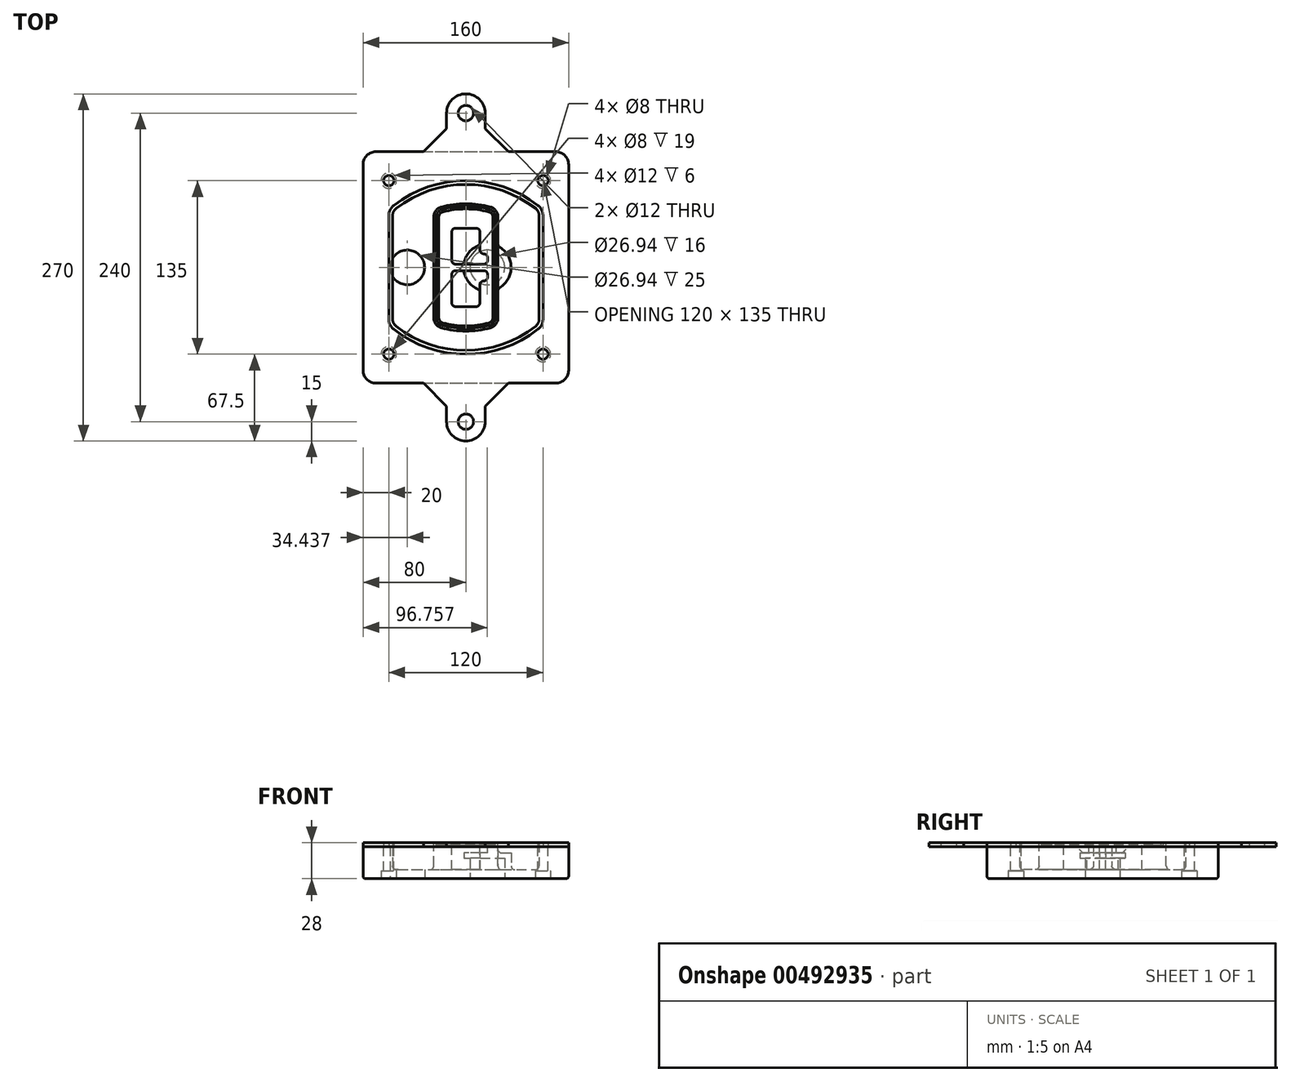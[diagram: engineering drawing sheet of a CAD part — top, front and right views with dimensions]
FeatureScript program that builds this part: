
annotation { "Feature Type Name" : "Feature", "Feature Type Description" : "" }
export const myFeature = defineFeature(function(context is Context, id is Id, definition is map)
    precondition{}
    {
        {
            var Q0;
            Q0=qCreatedBy(makeId("Top.planeOp"),FACE);
            var sketch = newSketch(context, id + "F0", { "sketchPlane" : qUnion([Q0])});
            skPoint(sketch, "E0.rect.middle", {"position": v(0, 0) * mm});
            skLineSegment(sketch, "E1.bottom", {"start": v(-70, -90) * mm, "end": v(70, -90) * mm});
            skLineSegment(sketch, "E1.top", {"start": v(-70, 90) * mm, "end": v(70, 90) * mm});
            skLineSegment(sketch, "E1.left", {"start": v(-80, -80) * mm, "end": v(-80, 80) * mm});
            skLineSegment(sketch, "E1.right", {"start": v(80, -80) * mm, "end": v(80, 80) * mm});
            skLineSegment(sketch, "E2", {"start": v(-80, 90) * mm, "end": v(80, -90) * mm, "construction": true});
            skLineSegment(sketch, "E3", {"start": v(80, 90) * mm, "end": v(-80, -90) * mm, "construction": true});
            skCircle(sketch, "E4", {"center": v(-60, 67.5) * mm, "radius": 4 * mm});
            skCircle(sketch, "E5", {"center": v(60, 67.5) * mm, "radius": 4 * mm});
            skCircle(sketch, "E6", {"center": v(60, -67.5) * mm, "radius": 4 * mm});
            skCircle(sketch, "E7", {"center": v(-60, -67.5) * mm, "radius": 4 * mm});
            skLineSegment(sketch, "E8", {"start": v(-60, 67.5) * mm, "end": v(60, 67.5) * mm, "construction": true});
            skLineSegment(sketch, "E9", {"start": v(60, 67.5) * mm, "end": v(60, -67.5) * mm, "construction": true});
            skLineSegment(sketch, "E10", {"start": v(60, -67.5) * mm, "end": v(-60, -67.5) * mm, "construction": true});
            skLineSegment(sketch, "E11", {"start": v(-60, -67.5) * mm, "end": v(-60, 67.5) * mm, "construction": true});
            skLineSegment(sketch, "E12", {"start": v(-60, 40.3) * mm, "end": v(-60, -40.3) * mm});
            skLineSegment(sketch, "E13", {"start": v(60, 40.3) * mm, "end": v(60, -40.3) * mm});
            skArc(sketch, "E14", {"start": v(56.15, 48.18) * mm, "mid": v(0, 67.5) * mm, "end": v(-56.15, 48.18) * mm});
            skArc(sketch, "E15", {"start": v(-56.15, -48.18) * mm, "mid": v(0, -67.5) * mm, "end": v(56.15, -48.18) * mm});
            skLineSegment(sketch, "E16", {"start": v(-60, 0) * mm, "end": v(60, 0) * mm, "construction": true});
            skPoint(sketch, "E17.visualSharp", {"position": v(-60, -45) * mm});
            skArc(sketch, "E17.filletArc", {"start": v(-60, -40.3) * mm, "mid": v(-58.99, -44.68) * mm, "end": v(-56.15, -48.18) * mm});
            skPoint(sketch, "E18.visualSharp", {"position": v(-60, 45) * mm});
            skArc(sketch, "E18.filletArc", {"start": v(-56.15, 48.18) * mm, "mid": v(-58.99, 44.68) * mm, "end": v(-60, 40.3) * mm});
            skPoint(sketch, "E19.visualSharp", {"position": v(60, 45) * mm});
            skArc(sketch, "E19.filletArc", {"start": v(60, 40.3) * mm, "mid": v(58.99, 44.68) * mm, "end": v(56.15, 48.18) * mm});
            skPoint(sketch, "E20.visualSharp", {"position": v(60, -45) * mm});
            skArc(sketch, "E20.filletArc", {"start": v(56.15, -48.18) * mm, "mid": v(58.99, -44.68) * mm, "end": v(60, -40.3) * mm});
            skPoint(sketch, "E21.visualSharp", {"position": v(-80, 90) * mm});
            skArc(sketch, "E21.filletArc", {"start": v(-70, 90) * mm, "mid": v(-77.07, 87.07) * mm, "end": v(-80, 80) * mm});
            skPoint(sketch, "E22.visualSharp", {"position": v(80, 90) * mm});
            skArc(sketch, "E22.filletArc", {"start": v(80, 80) * mm, "mid": v(77.07, 87.07) * mm, "end": v(70, 90) * mm});
            skPoint(sketch, "E23.visualSharp", {"position": v(80, -90) * mm});
            skArc(sketch, "E23.filletArc", {"start": v(70, -90) * mm, "mid": v(77.07, -87.07) * mm, "end": v(80, -80) * mm});
            skPoint(sketch, "E24.visualSharp", {"position": v(-80, -90) * mm});
            skArc(sketch, "E24.filletArc", {"start": v(-80, -80) * mm, "mid": v(-77.07, -87.07) * mm, "end": v(-70, -90) * mm});
            skArc(sketch, "E25.0", {"start": v(57, 40.3) * mm, "mid": v(56.3, 43.36) * mm, "end": v(54.3, 45.81) * mm});
            skLineSegment(sketch, "E25.1", {"start": v(57, 40.3) * mm, "end": v(57, -40.3) * mm});
            skArc(sketch, "E25.2", {"start": v(54.3, -45.81) * mm, "mid": v(56.3, -43.36) * mm, "end": v(57, -40.3) * mm});
            skArc(sketch, "E25.3", {"start": v(-54.3, -45.81) * mm, "mid": v(0, -64.5) * mm, "end": v(54.3, -45.81) * mm});
            skArc(sketch, "E25.4", {"start": v(-57, -40.3) * mm, "mid": v(-56.3, -43.36) * mm, "end": v(-54.3, -45.81) * mm});
            skArc(sketch, "E25.5", {"start": v(54.3, 45.81) * mm, "mid": v(0, 64.5) * mm, "end": v(-54.3, 45.81) * mm});
            skLineSegment(sketch, "E25.6", {"start": v(-57, 40.3) * mm, "end": v(-57, -40.3) * mm});
            skArc(sketch, "E25.7", {"start": v(-54.3, 45.81) * mm, "mid": v(-56.3, 43.36) * mm, "end": v(-57, 40.3) * mm});
            skArc(sketch, "E26.0", {"start": v(-58.62, 51.33) * mm, "mid": v(-62.58, 46.43) * mm, "end": v(-64, 40.3) * mm});
            skArc(sketch, "E26.1", {"start": v(58.62, 51.33) * mm, "mid": v(0, 71.5) * mm, "end": v(-58.62, 51.33) * mm});
            skArc(sketch, "E26.2", {"start": v(64, 40.3) * mm, "mid": v(62.58, 46.43) * mm, "end": v(58.62, 51.33) * mm});
            skLineSegment(sketch, "E26.3", {"start": v(64, 40.3) * mm, "end": v(64, -40.3) * mm});
            skArc(sketch, "E26.4", {"start": v(58.62, -51.33) * mm, "mid": v(62.58, -46.43) * mm, "end": v(64, -40.3) * mm});
            skLineSegment(sketch, "E26.5", {"start": v(-64, 40.3) * mm, "end": v(-64, -40.3) * mm});
            skArc(sketch, "E26.6", {"start": v(-58.62, -51.33) * mm, "mid": v(0, -71.5) * mm, "end": v(58.62, -51.33) * mm});
            skArc(sketch, "E26.7", {"start": v(-64, -40.3) * mm, "mid": v(-62.58, -46.43) * mm, "end": v(-58.62, -51.33) * mm});
            skSolve(sketch);
        }
        {
            var Q0;
            Q0=makeQuery(id+"F0.imprint","IMPRINT",FACE,{"disambiguationData":[TD([[makeQuery(id+"F0.imprint","IMPRINT",EDGE,{"derivedFrom":sQuery(id+"F0.wireOp",EDGE,"E1.bottom")}),1.0]])]});
            var Q1;
            Q1=makeQuery(id+"F0.imprint","IMPRINT",FACE,{"disambiguationData":[TD([[makeQuery(id+"F0.imprint","IMPRINT",EDGE,{"derivedFrom":sQuery(id+"F0.wireOp",EDGE,"E12")}),1.0]])]});
            var Q2;
            Q2=makeQuery(id+"F0.imprint","IMPRINT",FACE,{"disambiguationData":[TD([[makeQuery(id+"F0.imprint","IMPRINT",EDGE,{"derivedFrom":sQuery(id+"F0.wireOp",EDGE,"E25.0")}),1.0]])]});
            var Q3;
            Q3=makeQuery(id+"F0.imprint","IMPRINT",FACE,{"disambiguationData":[TD([[makeQuery(id+"F0.imprint","IMPRINT",EDGE,{"derivedFrom":sQuery(id+"F0.wireOp",EDGE,"E12")}),-1.0]])]});
            extrude(context, id + "F1", {"entities" : qUnion([Q0, Q1, Q2, Q3]), "oppositeDirection" : true, "depth" : 25 * mm});
        }
        {
            var Q0;
            Q0=makeQuery(id+"F0.imprint","IMPRINT",FACE,{"disambiguationData":[TD([[makeQuery(id+"F0.imprint","IMPRINT",EDGE,{"derivedFrom":sQuery(id+"F0.wireOp",EDGE,"E12")}),1.0]])]});
            extrude(context, id + "F2", {"entities" : qUnion([Q0]), "operationType" : NewBodyOperationType.ADD, "depth" : 3 * mm});
        }
        {
            var Q0;
            Q0=makeQuery(id+"F0.imprint","IMPRINT",FACE,{"disambiguationData":[TD([[makeQuery(id+"F0.imprint","IMPRINT",EDGE,{"derivedFrom":sQuery(id+"F0.wireOp",EDGE,"E25.0")}),1.0]])]});
            extrude(context, id + "F3", {"entities" : qUnion([Q0]), "operationType" : NewBodyOperationType.REMOVE, "oppositeDirection" : true, "depth" : 18 * mm});
        }
        {
            var Q0;
            Q0=makeQuery(id+"F2.opExtrude","CAP_FACE",FACE,{"disambiguationData":[OSD([sQuery(id+"F0.wireOp",EDGE,"E12"),sQuery(id+"F0.wireOp",EDGE,"E13"),sQuery(id+"F0.wireOp",EDGE,"E14"),sQuery(id+"F0.wireOp",EDGE,"E15"),sQuery(id+"F0.wireOp",EDGE,"E17.filletArc"),sQuery(id+"F0.wireOp",EDGE,"E18.filletArc"),sQuery(id+"F0.wireOp",EDGE,"E19.filletArc"),sQuery(id+"F0.wireOp",EDGE,"E20.filletArc"),sQuery(id+"F0.wireOp",EDGE,"E25.0"),sQuery(id+"F0.wireOp",EDGE,"E25.1"),sQuery(id+"F0.wireOp",EDGE,"E25.2"),sQuery(id+"F0.wireOp",EDGE,"E25.3"),sQuery(id+"F0.wireOp",EDGE,"E25.4"),sQuery(id+"F0.wireOp",EDGE,"E25.5"),sQuery(id+"F0.wireOp",EDGE,"E25.6"),sQuery(id+"F0.wireOp",EDGE,"E25.7")])],"isStart":false});
            var sketch = newSketch(context, id + "F4", { "sketchPlane" : qUnion([Q0])});
            skArc(sketch, "E27.0", {"start": v(-19.08, -46.97) * mm, "mid": v(0, -49.5) * mm, "end": v(19.08, -46.97) * mm});
            skArc(sketch, "E28.0", {"start": v(19.08, 46.97) * mm, "mid": v(0, 49.5) * mm, "end": v(-19.08, 46.97) * mm});
            skLineSegment(sketch, "E29", {"start": v(-25, 39.25) * mm, "end": v(-25, -39.25) * mm});
            skLineSegment(sketch, "E30", {"start": v(25, 39.25) * mm, "end": v(25, -39.25) * mm});
            skLineSegment(sketch, "E31", {"start": v(-25, 45.1) * mm, "end": v(25, 45.1) * mm, "construction": true});
            skLineSegment(sketch, "E32", {"start": v(-25, -45.1) * mm, "end": v(25, -45.1) * mm, "construction": true});
            skPoint(sketch, "E33.visualSharp", {"position": v(-25, 45.1) * mm});
            skArc(sketch, "E33.filletArc", {"start": v(-19.08, 46.97) * mm, "mid": v(-23.35, 44.11) * mm, "end": v(-25, 39.25) * mm});
            skPoint(sketch, "E34.visualSharp", {"position": v(25, 45.1) * mm});
            skArc(sketch, "E34.filletArc", {"start": v(25, 39.25) * mm, "mid": v(23.35, 44.11) * mm, "end": v(19.08, 46.97) * mm});
            skPoint(sketch, "E35.visualSharp", {"position": v(25, -45.1) * mm});
            skArc(sketch, "E35.filletArc", {"start": v(19.08, -46.97) * mm, "mid": v(23.35, -44.11) * mm, "end": v(25, -39.25) * mm});
            skPoint(sketch, "E36.visualSharp", {"position": v(-25, -45.1) * mm});
            skArc(sketch, "E36.filletArc", {"start": v(-25, -39.25) * mm, "mid": v(-23.35, -44.11) * mm, "end": v(-19.08, -46.97) * mm});
            skArc(sketch, "E37.0", {"start": v(54.3, 45.81) * mm, "mid": v(0, 64.5) * mm, "end": v(-54.3, 45.81) * mm});
            skArc(sketch, "E37.1", {"start": v(-54.3, 45.81) * mm, "mid": v(-56.3, 43.36) * mm, "end": v(-57, 40.3) * mm});
            skLineSegment(sketch, "E37.2", {"start": v(-57, 40.3) * mm, "end": v(-57, -40.3) * mm});
            skArc(sketch, "E37.3", {"start": v(-57, -40.3) * mm, "mid": v(-56.3, -43.36) * mm, "end": v(-54.3, -45.81) * mm});
            skArc(sketch, "E37.4", {"start": v(-54.3, -45.81) * mm, "mid": v(0, -64.5) * mm, "end": v(54.3, -45.81) * mm});
            skArc(sketch, "E37.5", {"start": v(54.3, -45.81) * mm, "mid": v(56.3, -43.36) * mm, "end": v(57, -40.3) * mm});
            skLineSegment(sketch, "E37.6", {"start": v(57, 40.3) * mm, "end": v(57, -40.3) * mm});
            skArc(sketch, "E37.7", {"start": v(57, 40.3) * mm, "mid": v(56.3, 43.36) * mm, "end": v(54.3, 45.81) * mm});
            skLineSegment(sketch, "E38.0", {"start": v(23, 39.25) * mm, "end": v(23, -39.25) * mm});
            skArc(sketch, "E38.1", {"start": v(18.56, -45.04) * mm, "mid": v(21.76, -42.9) * mm, "end": v(23, -39.25) * mm});
            skArc(sketch, "E38.2", {"start": v(-18.56, -45.04) * mm, "mid": v(0, -47.5) * mm, "end": v(18.56, -45.04) * mm});
            skArc(sketch, "E38.3", {"start": v(-23, -39.25) * mm, "mid": v(-21.76, -42.9) * mm, "end": v(-18.56, -45.04) * mm});
            skLineSegment(sketch, "E38.4", {"start": v(-23, 39.25) * mm, "end": v(-23, -39.25) * mm});
            skArc(sketch, "E38.5", {"start": v(23, 39.25) * mm, "mid": v(21.76, 42.9) * mm, "end": v(18.56, 45.04) * mm});
            skArc(sketch, "E38.6", {"start": v(-18.56, 45.04) * mm, "mid": v(-21.76, 42.9) * mm, "end": v(-23, 39.25) * mm});
            skArc(sketch, "E38.7", {"start": v(18.56, 45.04) * mm, "mid": v(0, 47.5) * mm, "end": v(-18.56, 45.04) * mm});
            skArc(sketch, "E39.0", {"start": v(21, 39.25) * mm, "mid": v(20.18, 41.68) * mm, "end": v(18.04, 43.1) * mm});
            skLineSegment(sketch, "E39.1", {"start": v(21, 39.25) * mm, "end": v(21, -39.25) * mm});
            skArc(sketch, "E39.2", {"start": v(18.04, -43.1) * mm, "mid": v(20.18, -41.68) * mm, "end": v(21, -39.25) * mm});
            skArc(sketch, "E39.3", {"start": v(-18.04, -43.1) * mm, "mid": v(0, -45.5) * mm, "end": v(18.04, -43.1) * mm});
            skArc(sketch, "E39.4", {"start": v(-21, -39.25) * mm, "mid": v(-20.18, -41.68) * mm, "end": v(-18.04, -43.1) * mm});
            skArc(sketch, "E39.5", {"start": v(18.04, 43.1) * mm, "mid": v(0, 45.5) * mm, "end": v(-18.04, 43.1) * mm});
            skLineSegment(sketch, "E39.6", {"start": v(-21, 39.25) * mm, "end": v(-21, -39.25) * mm});
            skArc(sketch, "E39.7", {"start": v(-18.04, 43.1) * mm, "mid": v(-20.18, 41.68) * mm, "end": v(-21, 39.25) * mm});
            skLineSegment(sketch, "E40", {"start": v(-25, 0) * mm, "end": v(25, 0) * mm, "construction": true});
            skLineSegment(sketch, "E41", {"start": v(-11, 5.5) * mm, "end": v(-11, 27.5) * mm});
            skLineSegment(sketch, "E42", {"start": v(-8, 30.5) * mm, "end": v(8, 30.5) * mm});
            skLineSegment(sketch, "E43", {"start": v(11, 27.5) * mm, "end": v(11, 13.5) * mm});
            skLineSegment(sketch, "E44", {"start": v(14, 10.5) * mm, "end": v(14, 10.5) * mm});
            skLineSegment(sketch, "E45", {"start": v(17, 7.5) * mm, "end": v(17, 5.5) * mm});
            skLineSegment(sketch, "E46", {"start": v(14, 2.5) * mm, "end": v(-8, 2.5) * mm});
            skPoint(sketch, "E47.visualSharp", {"position": v(-11, 30.5) * mm});
            skArc(sketch, "E47.filletArc", {"start": v(-8, 30.5) * mm, "mid": v(-10.12, 29.62) * mm, "end": v(-11, 27.5) * mm});
            skPoint(sketch, "E48.visualSharp", {"position": v(11, 30.5) * mm});
            skArc(sketch, "E48.filletArc", {"start": v(11, 27.5) * mm, "mid": v(10.12, 29.62) * mm, "end": v(8, 30.5) * mm});
            skPoint(sketch, "E49.visualSharp", {"position": v(11, 10.5) * mm});
            skArc(sketch, "E49.filletArc", {"start": v(11, 13.5) * mm, "mid": v(11.88, 11.38) * mm, "end": v(14, 10.5) * mm});
            skPoint(sketch, "E50.visualSharp", {"position": v(17, 10.5) * mm});
            skArc(sketch, "E50.filletArc", {"start": v(17, 7.5) * mm, "mid": v(16.12, 9.62) * mm, "end": v(14, 10.5) * mm});
            skPoint(sketch, "E51.visualSharp", {"position": v(17, 2.5) * mm});
            skArc(sketch, "E51.filletArc", {"start": v(14, 2.5) * mm, "mid": v(16.12, 3.38) * mm, "end": v(17, 5.5) * mm});
            skPoint(sketch, "E52.visualSharp", {"position": v(-11, 2.5) * mm});
            skArc(sketch, "E52.filletArc", {"start": v(-11, 5.5) * mm, "mid": v(-10.12, 3.38) * mm, "end": v(-8, 2.5) * mm});
            skLineSegment(sketch, "E53.0.MirrorCS", {"start": v(14, -2.5) * mm, "end": v(-8, -2.5) * mm});
            skArc(sketch, "E54.0.MirrorCS", {"start": v(-11, -5.5) * mm, "mid": v(-10.12, -3.38) * mm, "end": v(-8, -2.5) * mm});
            skLineSegment(sketch, "E55.0.MirrorCS", {"start": v(-11, -5.5) * mm, "end": v(-11, -27.5) * mm});
            skArc(sketch, "E56.0.MirrorCS", {"start": v(-8, -30.5) * mm, "mid": v(-10.12, -29.62) * mm, "end": v(-11, -27.5) * mm});
            skLineSegment(sketch, "E57.0.MirrorCS", {"start": v(-8, -30.5) * mm, "end": v(8, -30.5) * mm});
            skArc(sketch, "E58.0.MirrorCS", {"start": v(11, -27.5) * mm, "mid": v(10.12, -29.62) * mm, "end": v(8, -30.5) * mm});
            skLineSegment(sketch, "E59.0.MirrorCS", {"start": v(11, -27.5) * mm, "end": v(11, -13.5) * mm});
            skArc(sketch, "E60.0.MirrorCS", {"start": v(11, -13.5) * mm, "mid": v(11.88, -11.38) * mm, "end": v(14, -10.5) * mm});
            skArc(sketch, "E61.0.MirrorCS", {"start": v(17, -7.5) * mm, "mid": v(16.12, -9.62) * mm, "end": v(14, -10.5) * mm});
            skLineSegment(sketch, "E62.0.MirrorCS", {"start": v(17, -7.5) * mm, "end": v(17, -5.5) * mm});
            skArc(sketch, "E63.0.MirrorCS", {"start": v(14, -2.5) * mm, "mid": v(16.12, -3.38) * mm, "end": v(17, -5.5) * mm});
            skSolve(sketch);
        }
        {
            var Q0;
            Q0=makeQuery(id+"F4.imprint","IMPRINT",FACE,{"disambiguationData":[TD([[makeQuery(id+"F4.imprint","IMPRINT",EDGE,{"derivedFrom":sQuery(id+"F4.wireOp",EDGE,"E27.0")}),1.0]])]});
            var Q1;
            Q1=makeQuery(id+"F4.imprint","IMPRINT",FACE,{"disambiguationData":[TD([[makeQuery(id+"F4.imprint","IMPRINT",EDGE,{"derivedFrom":sQuery(id+"F4.wireOp",EDGE,"E38.0")}),-1.0]])]});
            var Q2;
            Q2=makeQuery(id+"F4.imprint","IMPRINT",FACE,{"disambiguationData":[TD([[makeQuery(id+"F4.imprint","IMPRINT",EDGE,{"derivedFrom":sQuery(id+"F4.wireOp",EDGE,"E39.0")}),1.0]])]});
            extrude(context, id + "F5", {"entities" : qUnion([Q0, Q1, Q2]), "operationType" : NewBodyOperationType.ADD, "endBound" : BoundingType.UP_TO_NEXT, "oppositeDirection" : true, "depth" : 25 * mm});
        }
        {
            var Q0;
            Q0=makeQuery(id+"F4.imprint","IMPRINT",FACE,{"disambiguationData":[TD([[makeQuery(id+"F4.imprint","IMPRINT",EDGE,{"derivedFrom":sQuery(id+"F4.wireOp",EDGE,"E38.0")}),-1.0]])]});
            extrude(context, id + "F6", {"entities" : qUnion([Q0]), "operationType" : NewBodyOperationType.REMOVE, "oppositeDirection" : true, "depth" : 2 * mm});
        }
        {
            var Q0;
            Q0=makeQuery(id+"F1.opExtrude","CAP_FACE",FACE,{"disambiguationData":[OSD([sQuery(id+"F0.wireOp",EDGE,"E1.bottom"),sQuery(id+"F0.wireOp",EDGE,"E1.top"),sQuery(id+"F0.wireOp",EDGE,"E1.left"),sQuery(id+"F0.wireOp",EDGE,"E1.right"),sQuery(id+"F0.wireOp",EDGE,"E4"),sQuery(id+"F0.wireOp",EDGE,"E5"),sQuery(id+"F0.wireOp",EDGE,"E6"),sQuery(id+"F0.wireOp",EDGE,"E7"),sQuery(id+"F0.wireOp",EDGE,"E21.filletArc"),sQuery(id+"F0.wireOp",EDGE,"E22.filletArc"),sQuery(id+"F0.wireOp",EDGE,"E23.filletArc"),sQuery(id+"F0.wireOp",EDGE,"E24.filletArc")])],"isStart":false});
            var sketch = newSketch(context, id + "F7", { "sketchPlane" : qUnion([Q0])});
            skCircle(sketch, "E64", {"center": v(16.76, 0) * mm, "radius": 13.47 * mm});
            skCircle(sketch, "E65", {"center": v(-45.56, 0) * mm, "radius": 13.47 * mm});
            skLineSegment(sketch, "E66", {"start": v(80, 0) * mm, "end": v(-80, 0) * mm});
            skCircle(sketch, "E67", {"center": v(16.76, 0) * mm, "radius": 18.47 * mm});
            skCircle(sketch, "E68", {"center": v(60, -67.5) * mm, "radius": 6 * mm});
            skCircle(sketch, "E69", {"center": v(-60, -67.5) * mm, "radius": 6 * mm});
            skCircle(sketch, "E70", {"center": v(-60, 67.5) * mm, "radius": 6 * mm});
            skCircle(sketch, "E71", {"center": v(60, 67.5) * mm, "radius": 6 * mm});
            skSolve(sketch);
        }
        {
            var Q0;
            {var subQ1=sQuery(id+"F7.wireOp",EDGE,"E66");var subQ4=sQuery(id+"F7.wireOp",EDGE,"E64");var subQ6=makeQuery(id+"F7.imprint","INTERSECT",VERTEX,{"disambiguationData":[OD(0.0)],"derivedFrom":[subQ4,subQ1]});Q0=makeQuery(id+"F7.imprint","IMPRINT",FACE,{"disambiguationData":[TD([[makeQuery(id+"F7.imprint","IMPRINT",EDGE,{"disambiguationData":[TD([[subQ6,-1.0]])],"derivedFrom":subQ4}),-1.0]])]});}
            var Q1;
            {var subQ0=sQuery(id+"F7.wireOp",EDGE,"E66");var subQ1=sQuery(id+"F7.wireOp",EDGE,"E64");var subQ3=makeQuery(id+"F7.imprint","INTERSECT",VERTEX,{"disambiguationData":[OD(0.0)],"derivedFrom":[subQ1,subQ0]});Q1=makeQuery(id+"F7.imprint","IMPRINT",FACE,{"disambiguationData":[TD([[makeQuery(id+"F7.imprint","IMPRINT",EDGE,{"disambiguationData":[TD([[subQ3,-1.0]])],"derivedFrom":subQ1}),1.0]])]});}
            var Q2;
            {var subQ0=sQuery(id+"F7.wireOp",EDGE,"E66");var subQ1=sQuery(id+"F7.wireOp",EDGE,"E64");var subQ3=makeQuery(id+"F7.imprint","INTERSECT",VERTEX,{"disambiguationData":[OD(0.0)],"derivedFrom":[subQ1,subQ0]});Q2=makeQuery(id+"F7.imprint","IMPRINT",FACE,{"disambiguationData":[TD([[makeQuery(id+"F7.imprint","IMPRINT",EDGE,{"disambiguationData":[TD([[subQ3,1.0]])],"derivedFrom":subQ1}),1.0]])]});}
            var Q3;
            {var subQ1=sQuery(id+"F7.wireOp",EDGE,"E66");var subQ4=sQuery(id+"F7.wireOp",EDGE,"E64");var subQ6=makeQuery(id+"F7.imprint","INTERSECT",VERTEX,{"disambiguationData":[OD(0.0)],"derivedFrom":[subQ4,subQ1]});Q3=makeQuery(id+"F7.imprint","IMPRINT",FACE,{"disambiguationData":[TD([[makeQuery(id+"F7.imprint","IMPRINT",EDGE,{"disambiguationData":[TD([[subQ6,1.0]])],"derivedFrom":subQ4}),-1.0]])]});}
            extrude(context, id + "F8", {"entities" : qUnion([Q0, Q1, Q2, Q3]), "operationType" : NewBodyOperationType.ADD, "oppositeDirection" : true, "depth" : 20 * mm});
        }
        {
            var Q0;
            {var subQ0=sQuery(id+"F7.wireOp",EDGE,"E66");var subQ1=sQuery(id+"F7.wireOp",EDGE,"E64");var subQ3=makeQuery(id+"F7.imprint","INTERSECT",VERTEX,{"disambiguationData":[OD(0.0)],"derivedFrom":[subQ1,subQ0]});Q0=makeQuery(id+"F7.imprint","IMPRINT",FACE,{"disambiguationData":[TD([[makeQuery(id+"F7.imprint","IMPRINT",EDGE,{"disambiguationData":[TD([[subQ3,-1.0]])],"derivedFrom":subQ1}),1.0]])]});}
            var Q1;
            {var subQ0=sQuery(id+"F7.wireOp",EDGE,"E66");var subQ1=sQuery(id+"F7.wireOp",EDGE,"E64");var subQ3=makeQuery(id+"F7.imprint","INTERSECT",VERTEX,{"disambiguationData":[OD(0.0)],"derivedFrom":[subQ1,subQ0]});Q1=makeQuery(id+"F7.imprint","IMPRINT",FACE,{"disambiguationData":[TD([[makeQuery(id+"F7.imprint","IMPRINT",EDGE,{"disambiguationData":[TD([[subQ3,1.0]])],"derivedFrom":subQ1}),1.0]])]});}
            extrude(context, id + "F9", {"entities" : qUnion([Q0, Q1]), "operationType" : NewBodyOperationType.REMOVE, "oppositeDirection" : true, "depth" : 16 * mm});
        }
        {
            var Q0;
            {var subQ0=sQuery(id+"F7.wireOp",EDGE,"E66");var subQ1=sQuery(id+"F7.wireOp",EDGE,"E65");var subQ3=makeQuery(id+"F7.imprint","INTERSECT",VERTEX,{"disambiguationData":[OD(0.0)],"derivedFrom":[subQ1,subQ0]});Q0=makeQuery(id+"F7.imprint","IMPRINT",FACE,{"disambiguationData":[TD([[makeQuery(id+"F7.imprint","IMPRINT",EDGE,{"disambiguationData":[TD([[subQ3,-1.0]])],"derivedFrom":subQ1}),1.0]])]});}
            var Q1;
            {var subQ0=sQuery(id+"F7.wireOp",EDGE,"E66");var subQ1=sQuery(id+"F7.wireOp",EDGE,"E65");var subQ3=makeQuery(id+"F7.imprint","INTERSECT",VERTEX,{"disambiguationData":[OD(0.0)],"derivedFrom":[subQ1,subQ0]});Q1=makeQuery(id+"F7.imprint","IMPRINT",FACE,{"disambiguationData":[TD([[makeQuery(id+"F7.imprint","IMPRINT",EDGE,{"disambiguationData":[TD([[subQ3,1.0]])],"derivedFrom":subQ1}),1.0]])]});}
            extrude(context, id + "F10", {"entities" : qUnion([Q0, Q1]), "operationType" : NewBodyOperationType.REMOVE, "oppositeDirection" : true, "depth" : 25 * mm});
        }
        {
            var Q0;
            Q0=makeQuery(id+"F7.imprint","IMPRINT",FACE,{"disambiguationData":[TD([[makeQuery(id+"F7.imprint","IMPRINT",EDGE,{"derivedFrom":sQuery(id+"F7.wireOp",EDGE,"E68")}),1.0]])]});
            var Q1;
            Q1=makeQuery(id+"F7.imprint","IMPRINT",FACE,{"disambiguationData":[TD([[makeQuery(id+"F7.imprint","IMPRINT",EDGE,{"derivedFrom":makeQuery(id+"F1.opExtrude","CAP_EDGE",EDGE,{"disambiguationData":[OSD([sQuery(id+"F0.wireOp",EDGE,"E5")])],"isStart":false})}),-1.0]])]});
            var Q2;
            Q2=makeQuery(id+"F7.imprint","IMPRINT",FACE,{"disambiguationData":[TD([[makeQuery(id+"F7.imprint","IMPRINT",EDGE,{"derivedFrom":sQuery(id+"F7.wireOp",EDGE,"E69")}),1.0]])]});
            var Q3;
            Q3=makeQuery(id+"F7.imprint","IMPRINT",FACE,{"disambiguationData":[TD([[makeQuery(id+"F7.imprint","IMPRINT",EDGE,{"derivedFrom":makeQuery(id+"F1.opExtrude","CAP_EDGE",EDGE,{"disambiguationData":[OSD([sQuery(id+"F0.wireOp",EDGE,"E4")])],"isStart":false})}),-1.0]])]});
            var Q4;
            Q4=makeQuery(id+"F7.imprint","IMPRINT",FACE,{"disambiguationData":[TD([[makeQuery(id+"F7.imprint","IMPRINT",EDGE,{"derivedFrom":sQuery(id+"F7.wireOp",EDGE,"E70")}),1.0]])]});
            var Q5;
            Q5=makeQuery(id+"F7.imprint","IMPRINT",FACE,{"disambiguationData":[TD([[makeQuery(id+"F7.imprint","IMPRINT",EDGE,{"derivedFrom":makeQuery(id+"F1.opExtrude","CAP_EDGE",EDGE,{"disambiguationData":[OSD([sQuery(id+"F0.wireOp",EDGE,"E7")])],"isStart":false})}),-1.0]])]});
            var Q6;
            Q6=makeQuery(id+"F7.imprint","IMPRINT",FACE,{"disambiguationData":[TD([[makeQuery(id+"F7.imprint","IMPRINT",EDGE,{"derivedFrom":sQuery(id+"F7.wireOp",EDGE,"E71")}),1.0]])]});
            var Q7;
            Q7=makeQuery(id+"F7.imprint","IMPRINT",FACE,{"disambiguationData":[TD([[makeQuery(id+"F7.imprint","IMPRINT",EDGE,{"derivedFrom":makeQuery(id+"F1.opExtrude","CAP_EDGE",EDGE,{"disambiguationData":[OSD([sQuery(id+"F0.wireOp",EDGE,"E6")])],"isStart":false})}),-1.0]])]});
            extrude(context, id + "F11", {"entities" : qUnion([Q0, Q1, Q2, Q3, Q4, Q5, Q6, Q7]), "operationType" : NewBodyOperationType.REMOVE, "oppositeDirection" : true, "depth" : 6 * mm});
        }
        {
            var Q0;
            Q0=makeQuery(id+"F9.boolean.opBoolean","COPY",FACE,{"derivedFrom":makeQuery(id+"F9.opExtrude","CAP_FACE",FACE,{"disambiguationData":[OSD([sQuery(id+"F7.wireOp",EDGE,"E64")])],"isStart":false})});
            var sketch = newSketch(context, id + "F12", { "sketchPlane" : qUnion([Q0])});
            skArc(sketch, "E72.0", {"start": v(11, 17.55) * mm, "mid": v(2.57, 11.82) * mm, "end": v(-1.54, 2.5) * mm});
            skArc(sketch, "E72.1", {"start": v(-1.54, -2.5) * mm, "mid": v(2.57, -11.82) * mm, "end": v(11, -17.55) * mm});
            skLineSegment(sketch, "E73", {"start": v(-1.54, -2.5) * mm, "end": v(14, -2.5) * mm});
            skLineSegment(sketch, "E74.0", {"start": v(14, 2.5) * mm, "end": v(-1.54, 2.5) * mm});
            skArc(sketch, "E74.1", {"start": v(14, 2.5) * mm, "mid": v(16.12, 3.38) * mm, "end": v(17, 5.5) * mm});
            skLineSegment(sketch, "E74.2", {"start": v(17, 7.5) * mm, "end": v(17, 5.5) * mm});
            skArc(sketch, "E74.3", {"start": v(17, 7.5) * mm, "mid": v(16.12, 9.62) * mm, "end": v(14, 10.5) * mm});
            skArc(sketch, "E74.4", {"start": v(11, 13.5) * mm, "mid": v(11.88, 11.38) * mm, "end": v(14, 10.5) * mm});
            skLineSegment(sketch, "E74.5", {"start": v(11, 17.55) * mm, "end": v(11, 13.5) * mm});
            skLineSegment(sketch, "E74.7", {"start": v(14, -2.5) * mm, "end": v(-1.54, -2.5) * mm});
            skArc(sketch, "E74.8", {"start": v(14, -2.5) * mm, "mid": v(16.12, -3.38) * mm, "end": v(17, -5.5) * mm});
            skLineSegment(sketch, "E74.9", {"start": v(17, -7.5) * mm, "end": v(17, -5.5) * mm});
            skArc(sketch, "E74.10", {"start": v(17, -7.5) * mm, "mid": v(16.12, -9.62) * mm, "end": v(14, -10.5) * mm});
            skArc(sketch, "E74.11", {"start": v(11, -13.5) * mm, "mid": v(11.88, -11.38) * mm, "end": v(14, -10.5) * mm});
            skLineSegment(sketch, "E74.12", {"start": v(11, -17.55) * mm, "end": v(11, -13.5) * mm});
            skPoint(sketch, "E75.orphan", {"position": v(11, -27.5) * mm});
            skPoint(sketch, "E76.orphan", {"position": v(-8, -2.5) * mm});
            skPoint(sketch, "E77.orphan", {"position": v(-8, 2.5) * mm});
            skPoint(sketch, "E78.orphan", {"position": v(11, 27.5) * mm});
            skSolve(sketch);
        }
        {
            var Q0;
            {var subQ7=sQuery(id+"F12.wireOp",EDGE,"E72.0");var subQ14=sQuery(id+"F12.wireOp",EDGE,"E72.1");var subQ16=sQuery(id+"F12.wireOp",EDGE,"E74.1");var subQ18=sQuery(id+"F12.wireOp",EDGE,"E74.8");Q0=qUnion([makeQuery(id+"F12.imprint","IMPRINT",FACE,{"disambiguationData":[TD([[makeQuery(id+"F12.imprint","IMPRINT",EDGE,{"derivedFrom":subQ7}),1.0]])]}),makeQuery(id+"F12.imprint","IMPRINT",FACE,{"disambiguationData":[TD([[makeQuery(id+"F12.imprint","IMPRINT",EDGE,{"derivedFrom":subQ14}),1.0]])]}),makeQuery(id+"F12.imprint","IMPRINT",FACE,{"disambiguationData":[TD([[makeQuery(id+"F12.imprint","IMPRINT",EDGE,{"derivedFrom":subQ16}),1.0]])]}),makeQuery(id+"F12.imprint","IMPRINT",FACE,{"disambiguationData":[TD([[makeQuery(id+"F12.imprint","IMPRINT",EDGE,{"derivedFrom":subQ18}),-1.0]])]})]);}
            var Q1;
            Q1=makeQuery(id+"F5.boolean.opBoolean","SPLIT",FACE,{"disambiguationData":[TD([makeQuery(id+"F5.opExtrude","SWEPT_FACE",FACE,{"disambiguationData":[OSD([sQuery(id+"F4.wireOp",EDGE,"E41")])]})])],"derivedFrom":makeQuery(id+"F3.boolean.opBoolean","COPY",FACE,{"derivedFrom":makeQuery(id+"F3.opExtrude","CAP_FACE",FACE,{"disambiguationData":[OSD([sQuery(id+"F0.wireOp",EDGE,"E25.0"),sQuery(id+"F0.wireOp",EDGE,"E25.1"),sQuery(id+"F0.wireOp",EDGE,"E25.2"),sQuery(id+"F0.wireOp",EDGE,"E25.3"),sQuery(id+"F0.wireOp",EDGE,"E25.4"),sQuery(id+"F0.wireOp",EDGE,"E25.5"),sQuery(id+"F0.wireOp",EDGE,"E25.6"),sQuery(id+"F0.wireOp",EDGE,"E25.7")])],"isStart":false})})});
            extrude(context, id + "F13", {"entities" : qUnion([Q0]), "operationType" : NewBodyOperationType.REMOVE, "endBound" : BoundingType.UP_TO_SURFACE, "endBoundEntityFace" : qUnion([Q1]), "depth" : 25 * mm});
        }
        {
            var Q0;
            Q0=makeQuery(id+"F3.boolean.opBoolean","COPY",EDGE,{"derivedFrom":makeQuery(id+"F3.opExtrude","CAP_EDGE",EDGE,{"disambiguationData":[OSD([sQuery(id+"F0.wireOp",EDGE,"E25.6")])],"isStart":false})});
            var Q1;
            Q1=makeQuery(id+"F8.boolean.opBoolean","INTERSECT",EDGE,{"derivedFrom":[makeQuery(id+"F5.opExtrude","SWEPT_FACE",FACE,{"disambiguationData":[OSD([sQuery(id+"F4.wireOp",EDGE,"E30")])]}),makeQuery(id+"F8.opExtrude","CAP_FACE",FACE,{"disambiguationData":[OSD([sQuery(id+"F7.wireOp",EDGE,"E67")])],"isStart":false})]});
            var Q2;
            Q2=makeQuery(id+"F8.boolean.opBoolean","INTERSECT",EDGE,{"disambiguationData":[OD(1.0)],"derivedFrom":[makeQuery(id+"F5.opExtrude","SWEPT_FACE",FACE,{"disambiguationData":[OSD([sQuery(id+"F4.wireOp",EDGE,"E30")])]}),makeQuery(id+"F8.opExtrude","SWEPT_FACE",FACE,{"disambiguationData":[OSD([sQuery(id+"F7.wireOp",EDGE,"E67")])]})]});
            var Q3;
            {var subQ0=sQuery(id+"F4.wireOp",EDGE,"E30");Q3=makeQuery(id+"F8.boolean.opBoolean","SPLIT",EDGE,{"disambiguationData":[TD([makeQuery(id+"F5.opExtrude","SWEPT_FACE",FACE,{"disambiguationData":[OSD([sQuery(id+"F4.wireOp",EDGE,"E35.filletArc")])]})])],"derivedFrom":makeQuery(id+"F5.opExtrude","CAP_EDGE",EDGE,{"disambiguationData":[OSD([subQ0])],"isStart":false})});}
            var Q4;
            {var subQ0=sQuery(id+"F0.wireOp",EDGE,"E25.7");var subQ1=sQuery(id+"F0.wireOp",EDGE,"E25.1");var subQ2=sQuery(id+"F0.wireOp",EDGE,"E25.6");var subQ3=sQuery(id+"F0.wireOp",EDGE,"E25.5");var subQ4=sQuery(id+"F0.wireOp",EDGE,"E25.4");var subQ5=sQuery(id+"F0.wireOp",EDGE,"E25.0");var subQ6=sQuery(id+"F0.wireOp",EDGE,"E25.2");var subQ7=sQuery(id+"F0.wireOp",EDGE,"E25.3");Q4=makeQuery(id+"F8.boolean.opBoolean","INTERSECT",EDGE,{"derivedFrom":[makeQuery(id+"F5.boolean.opBoolean","SPLIT",FACE,{"disambiguationData":[TD([makeQuery(id+"F2.opExtrude","SWEPT_FACE",FACE,{"disambiguationData":[OSD([subQ5])]})])],"derivedFrom":makeQuery(id+"F3.boolean.opBoolean","COPY",FACE,{"derivedFrom":makeQuery(id+"F3.opExtrude","CAP_FACE",FACE,{"disambiguationData":[OSD([subQ5,subQ1,subQ6,subQ7,subQ4,subQ3,subQ2,subQ0])],"isStart":false})})}),makeQuery(id+"F8.opExtrude","SWEPT_FACE",FACE,{"disambiguationData":[OSD([sQuery(id+"F7.wireOp",EDGE,"E67")])]})]});}
            var Q5;
            Q5=makeQuery(id+"F8.boolean.opBoolean","INTERSECT",EDGE,{"disambiguationData":[OD(0.0)],"derivedFrom":[makeQuery(id+"F5.opExtrude","SWEPT_FACE",FACE,{"disambiguationData":[OSD([sQuery(id+"F4.wireOp",EDGE,"E30")])]}),makeQuery(id+"F8.opExtrude","SWEPT_FACE",FACE,{"disambiguationData":[OSD([sQuery(id+"F7.wireOp",EDGE,"E67")])]})]});
            fillet(context, id + "F14", {"entities" : qUnion([Q0, Q1, Q2, Q3, Q4, Q5]), "radius" : 3 * mm, "tangentPropagation" : true, "allowEdgeOverflow" : false});
        }
        {
            var Q0;
            Q0=makeQuery(id+"F1.opExtrude","CAP_EDGE",EDGE,{"disambiguationData":[OSD([sQuery(id+"F0.wireOp",EDGE,"E1.bottom")])],"isStart":false});
            fillet(context, id + "F15", {"entities" : qUnion([Q0]), "radius" : 2 * mm, "tangentPropagation" : true, "allowEdgeOverflow" : false});
        }
        {
            var Q0;
            {var subQ0=sQuery(id+"F0.wireOp",EDGE,"E21.filletArc");var subQ1=sQuery(id+"F0.wireOp",EDGE,"E7");var subQ2=sQuery(id+"F0.wireOp",EDGE,"E6");var subQ3=sQuery(id+"F0.wireOp",EDGE,"E5");var subQ4=sQuery(id+"F0.wireOp",EDGE,"E4");var subQ5=sQuery(id+"F0.wireOp",EDGE,"E22.filletArc");var subQ6=sQuery(id+"F0.wireOp",EDGE,"E1.bottom");var subQ7=sQuery(id+"F0.wireOp",EDGE,"E1.right");var subQ8=sQuery(id+"F0.wireOp",EDGE,"E1.top");var subQ9=sQuery(id+"F0.wireOp",EDGE,"E1.left");var subQ10=sQuery(id+"F0.wireOp",EDGE,"E23.filletArc");var subQ11=sQuery(id+"F0.wireOp",EDGE,"E24.filletArc");Q0=makeQuery(id+"F2.boolean.opBoolean","SPLIT",FACE,{"disambiguationData":[TD([makeQuery(id+"F1.opExtrude","SWEPT_FACE",FACE,{"disambiguationData":[OSD([subQ6])]})])],"derivedFrom":makeQuery(id+"F1.opExtrude","CAP_FACE",FACE,{"disambiguationData":[OSD([subQ6,subQ8,subQ9,subQ7,subQ4,subQ3,subQ2,subQ1,subQ0,subQ5,subQ10,subQ11])],"isStart":true})});}
            var sketch = newSketch(context, id + "F16", { "sketchPlane" : qUnion([Q0])});
            skLineSegment(sketch, "E79", {"start": v(0, 90) * mm, "end": v(0, 120) * mm, "construction": true});
            skCircle(sketch, "E80", {"center": v(0, 120) * mm, "radius": 6 * mm});
            skLineSegment(sketch, "E81", {"start": v(-33, 90) * mm, "end": v(-15, 108) * mm});
            skLineSegment(sketch, "E82", {"start": v(-15, 108) * mm, "end": v(-15, 120) * mm});
            skLineSegment(sketch, "E83", {"start": v(33, 90) * mm, "end": v(15, 108) * mm});
            skLineSegment(sketch, "E84", {"start": v(15, 108) * mm, "end": v(15, 120) * mm});
            skArc(sketch, "E85", {"start": v(15, 120) * mm, "mid": v(0, 135) * mm, "end": v(-15, 120) * mm});
            skLineSegment(sketch, "E86", {"start": v(-80, 0) * mm, "end": v(80, 0) * mm, "construction": true});
            skLineSegment(sketch, "E87.MirrorCS", {"start": v(0, -90) * mm, "end": v(0, -120) * mm, "construction": true});
            skLineSegment(sketch, "E88.MirrorCS", {"start": v(15, -108) * mm, "end": v(15, -120) * mm});
            skCircle(sketch, "E89.MirrorC", {"center": v(0, -120) * mm, "radius": 6 * mm});
            skLineSegment(sketch, "E90.MirrorCS", {"start": v(-33, -90) * mm, "end": v(-15, -108) * mm});
            skLineSegment(sketch, "E91.MirrorCS", {"start": v(-15, -108) * mm, "end": v(-15, -120) * mm});
            skArc(sketch, "E92.MirrorCS", {"start": v(15, -120) * mm, "mid": v(0, -135) * mm, "end": v(-15, -120) * mm});
            skLineSegment(sketch, "E93.MirrorCS", {"start": v(33, -90) * mm, "end": v(15, -108) * mm});
            skSolve(sketch);
        }
        {
            var Q0;
            Q0=makeQuery(id+"F16.imprint","IMPRINT",FACE,{"disambiguationData":[TD([[makeQuery(id+"F16.imprint","IMPRINT",EDGE,{"derivedFrom":sQuery(id+"F16.wireOp",EDGE,"E80")}),-1.0]])]});
            var Q1;
            Q1=makeQuery(id+"F16.imprint","IMPRINT",FACE,{"disambiguationData":[TD([[makeQuery(id+"F16.imprint","IMPRINT",EDGE,{"derivedFrom":makeQuery(id+"F1.opExtrude","CAP_EDGE",EDGE,{"disambiguationData":[OSD([sQuery(id+"F0.wireOp",EDGE,"E1.left")])],"isStart":true})}),-1.0]])]});
            var Q2;
            Q2=makeQuery(id+"F16.imprint","IMPRINT",FACE,{"disambiguationData":[TD([[makeQuery(id+"F16.imprint","IMPRINT",EDGE,{"derivedFrom":sQuery(id+"F16.wireOp",EDGE,"E88.MirrorCS")}),-1.0]])]});
            var Q3;
            Q3=makeQuery(id+"F2.opExtrude","CAP_FACE",FACE,{"disambiguationData":[OSD([sQuery(id+"F0.wireOp",EDGE,"E12"),sQuery(id+"F0.wireOp",EDGE,"E13"),sQuery(id+"F0.wireOp",EDGE,"E14"),sQuery(id+"F0.wireOp",EDGE,"E15"),sQuery(id+"F0.wireOp",EDGE,"E17.filletArc"),sQuery(id+"F0.wireOp",EDGE,"E18.filletArc"),sQuery(id+"F0.wireOp",EDGE,"E19.filletArc"),sQuery(id+"F0.wireOp",EDGE,"E20.filletArc"),sQuery(id+"F0.wireOp",EDGE,"E25.0"),sQuery(id+"F0.wireOp",EDGE,"E25.1"),sQuery(id+"F0.wireOp",EDGE,"E25.2"),sQuery(id+"F0.wireOp",EDGE,"E25.3"),sQuery(id+"F0.wireOp",EDGE,"E25.4"),sQuery(id+"F0.wireOp",EDGE,"E25.5"),sQuery(id+"F0.wireOp",EDGE,"E25.6"),sQuery(id+"F0.wireOp",EDGE,"E25.7")])],"isStart":false});
            extrude(context, id + "F17", {"entities" : qUnion([Q0, Q1, Q2]), "endBound" : BoundingType.UP_TO_SURFACE, "endBoundEntityFace" : qUnion([Q3]), "depth" : 25 * mm});
        }
    });
